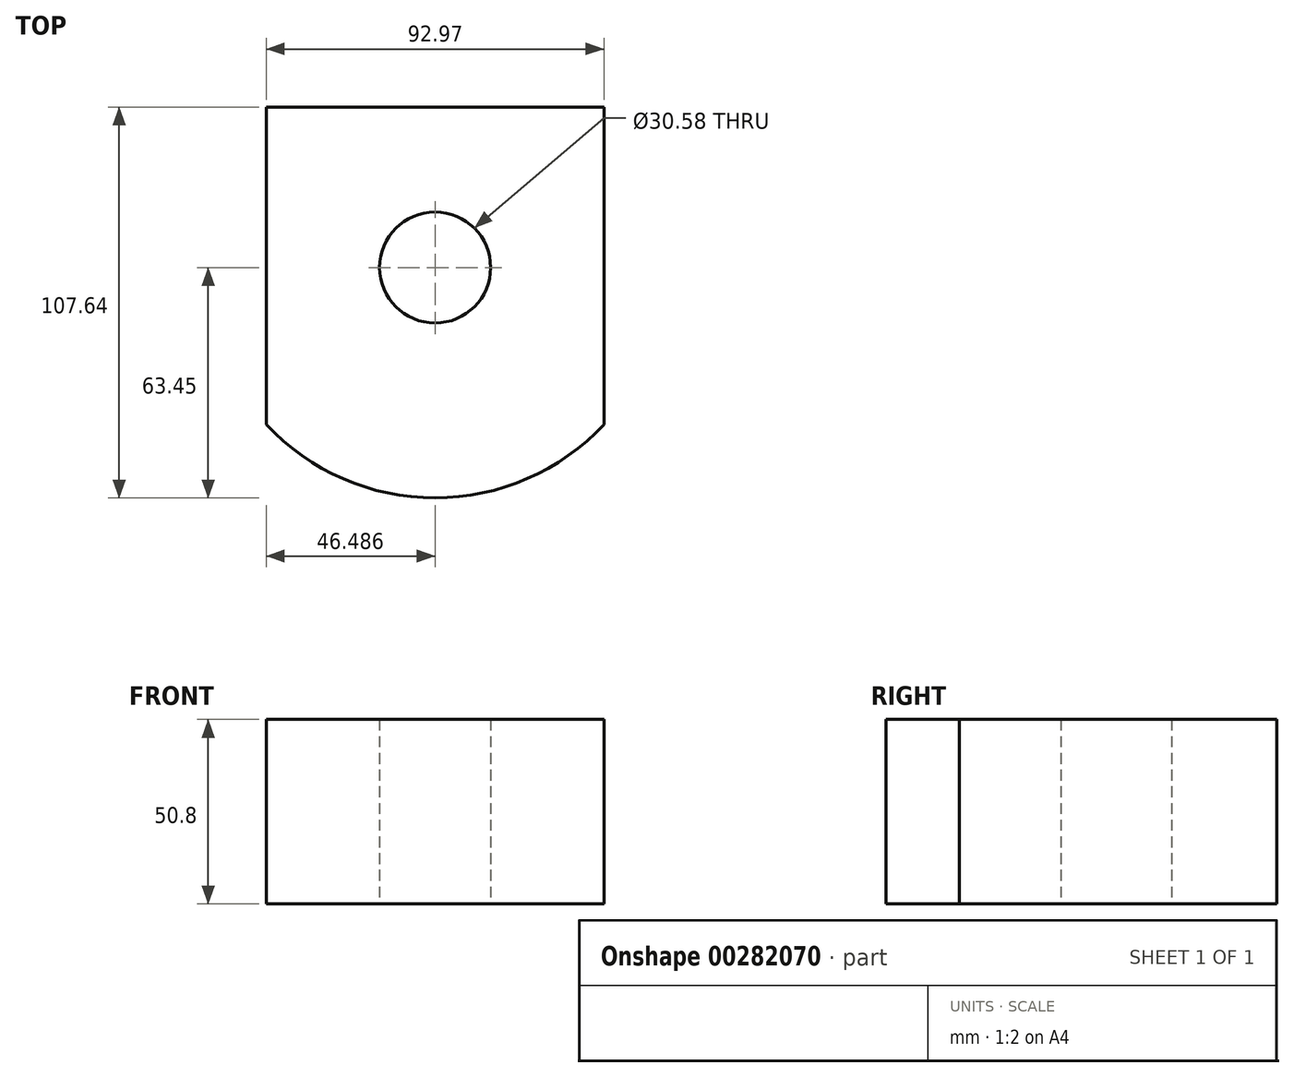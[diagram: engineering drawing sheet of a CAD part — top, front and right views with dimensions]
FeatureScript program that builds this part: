
annotation { "Feature Type Name" : "Feature", "Feature Type Description" : "" }
export const myFeature = defineFeature(function(context is Context, id is Id, definition is map)
    precondition{}
    {
        {
            var Q0;
            Q0=qCreatedBy(makeId("Top.planeOp"),FACE);
            var sketch = newSketch(context, id + "F0", { "sketchPlane" : qUnion([Q0])});
            skLineSegment(sketch, "E0.bottom", {"start": v(-55.63, 44.2) * mm, "end": v(37.34, 44.2) * mm});
            skLineSegment(sketch, "E0.top", {"start": v(-55.63, -43.18) * mm, "end": v(37.34, -43.18) * mm});
            skLineSegment(sketch, "E0.left", {"start": v(-55.63, 44.2) * mm, "end": v(-55.63, -43.18) * mm});
            skLineSegment(sketch, "E0.right", {"start": v(37.34, 44.2) * mm, "end": v(37.34, -43.18) * mm});
            skCircle(sketch, "E1", {"center": v(-9.14, 0) * mm, "radius": 15.3 * mm});
            skArc(sketch, "E2", {"start": v(-55.63, -43.18) * mm, "mid": v(-9.14, -63.45) * mm, "end": v(37.34, -43.18) * mm});
            skSolve(sketch);
        }
        {
            var Q0;
            Q0 = qSketchRegion(id + "F0", true);
            extrude(context, id + "F1", {"entities" : qUnion([Q0]), "depth" : 50.8 * mm});
        }
    });
